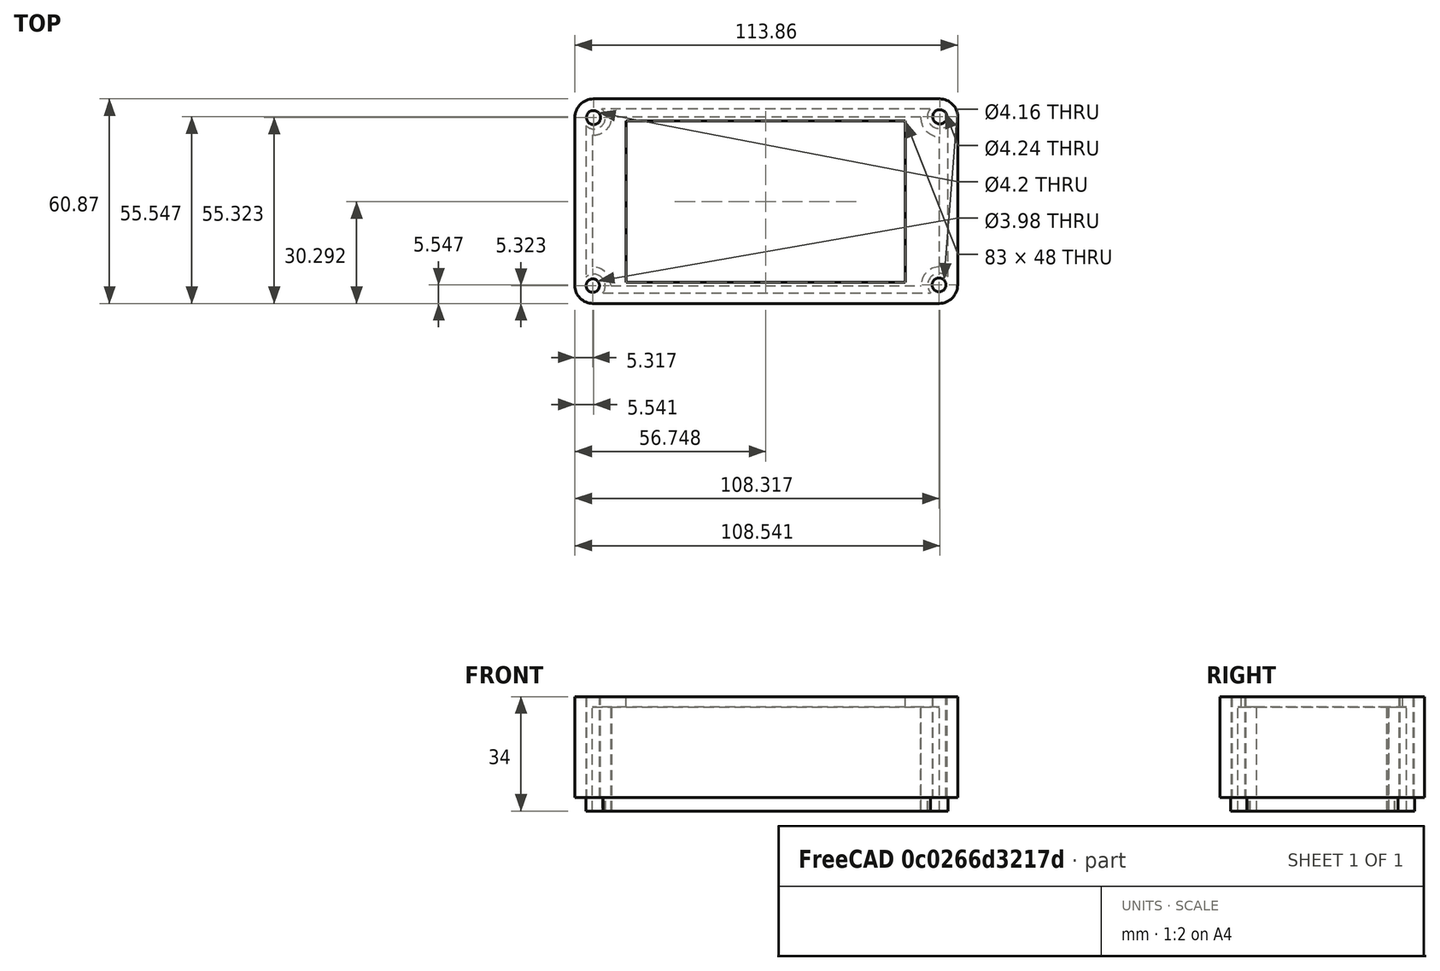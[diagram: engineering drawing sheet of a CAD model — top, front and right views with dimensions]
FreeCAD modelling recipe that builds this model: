
FCSTD DOCUMENT  (FreeCAD 0.18R4 (GitTag))
Label: uno
License: All rights reserved
LicenseURL: http://en.wikipedia.org/wiki/All_rights_reserved
objects: Sketcher::SketchObject×4, PartDesign::Pad×2, PartDesign::Pocket×2, PartDesign::Body×1, Mesh::Feature×1
note: 13 computed .brp shape members not serialized (recipe doc carries the construction recipe); baked Part::Feature solids carry a one-line shape summary decoded from their .brp

FEATURE [Sketcher::SketchObject] Sketch
  MapMode = 5
  Support = -> [XY_Plane]
  sketch-geometry (12):
    g0: LineSegment StartX=5.03716 StartY=-0.785506 StartZ=0 EndX=108.037 EndY=-0.785506 EndZ=0
    g1: LineSegment StartX=113.579 StartY=4.75676 StartZ=0 EndX=113.579 EndY=54.7568 EndZ=0
    g2: LineSegment StartX=108.261 StartY=60.0751 StartZ=0 EndX=5.26104 EndY=60.0751 EndZ=0
    g3: LineSegment StartX=-0.281219 StartY=54.5329 StartZ=0 EndX=-0.281219 EndY=4.53287 EndZ=0
    g4: ArcOfCircle CenterX=5.26104 CenterY=54.5329 CenterZ=0 NormalX=0 NormalY=0 NormalZ=1 AngleXU=0 Radius=5.54226 StartAngle=1.5708 EndAngle=3.14159
    g5: ArcOfCircle CenterX=108.261 CenterY=54.7568 CenterZ=0 NormalX=0 NormalY=0 NormalZ=1 AngleXU=0 Radius=5.31838 StartAngle=3e-16 EndAngle=1.5708
    g6: ArcOfCircle CenterX=5.03716 CenterY=4.53287 CenterZ=0 NormalX=0 NormalY=0 NormalZ=1 AngleXU=0 Radius=5.31838 StartAngle=3.14159 EndAngle=4.71239
    g7: ArcOfCircle CenterX=108.037 CenterY=4.75676 CenterZ=0 NormalX=0 NormalY=0 NormalZ=1 AngleXU=0 Radius=5.54226 StartAngle=4.71239 EndAngle=6.28319
    g8: Circle CenterX=5.03716 CenterY=4.53287 CenterZ=0 NormalX=0 NormalY=0 NormalZ=1 AngleXU=0 Radius=1.9886
    g9: Circle CenterX=108.037 CenterY=4.75676 CenterZ=0 NormalX=0 NormalY=0 NormalZ=1 AngleXU=0 Radius=2.07806
    g10: Circle CenterX=5.26104 CenterY=54.5329 CenterZ=0 NormalX=0 NormalY=0 NormalZ=1 AngleXU=0 Radius=2.0986
    g11: Circle CenterX=108.261 CenterY=54.7568 CenterZ=0 NormalX=0 NormalY=0 NormalZ=1 AngleXU=0 Radius=2.12051
  constraints (19):
    c: Horizontal(g0)
    c: Horizontal(g2)
    c: Vertical(g1)
    c: Vertical(g3)
    c: Tangent(g2,g4) = -1.5708
    c: Tangent(g3,g4) = -1.5708
    c: Tangent(g2,g5) = -1.5708
    c: Tangent(g1,g5) = -1.5708
    c: Tangent(g0,g6) = -1.5708
    c: Tangent(g3,g6) = -1.5708
    c: Tangent(g1,g7) = -1.5708
    c: Tangent(g0,g7) = -1.5708
    c: DistanceY(g3,g3) = 50
    c: DistanceX(g2,g2) = 103
    c: DistanceX(g0,g0) = 103
    c: Coincident(g8,g6)
    c: Coincident(g9,g7)
    c: Coincident(g10,g4)
    c: Coincident(g11,g5)
FEATURE [PartDesign::Pad] Pad
  Length = 30
  Length2 = 100
  Profile = -> Sketch
  Refine = true
  Type = 0
FEATURE [Sketcher::SketchObject] Sketch001
  MapMode = 5
  Placement = pos=(0,0,0) rot=(1,0,0;3.14159rad)
  Support = -> [Pad]
  sketch-geometry (8):
    g0: LineSegment StartX=8.07072 StartY=-2.40627 StartZ=0 EndX=105.522 EndY=-2.40627 EndZ=0
    g1: LineSegment StartX=110.632 StartY=-7.15837 StartZ=0 EndX=110.632 EndY=-52.2009 EndZ=0
    g2: LineSegment StartX=105.323 StartY=-57.0385 StartZ=0 EndX=7.70864 EndY=-57.0385 EndZ=0
    g3: LineSegment StartX=2.9358 StartY=-52.1381 StartZ=0 EndX=2.9358 EndY=-7.09059 EndZ=0
    g4: ArcOfCircle CenterX=5.24678 CenterY=-4.46729 CenterZ=0 NormalX=0 NormalY=0 NormalZ=1 AngleXU=0 Radius=3.49605 StartAngle=3.9902 EndAngle=6.91366
    g5: ArcOfCircle CenterX=5.36355 CenterY=-54.5481 CenterZ=0 NormalX=0 NormalY=0 NormalZ=1 AngleXU=0 Radius=3.42079 StartAngle=5.46773 EndAngle=8.64306
    g6: ArcOfCircle CenterX=108.149 CenterY=-4.7048 CenterZ=0 NormalX=0 NormalY=0 NormalZ=1 AngleXU=0 Radius=3.49068 StartAngle=2.4228 EndAngle=5.50373
    g7: ArcOfCircle CenterX=108.199 CenterY=-54.8624 CenterZ=0 NormalX=0 NormalY=0 NormalZ=1 AngleXU=0 Radius=3.60613 StartAngle=0.830175 EndAngle=3.78941
  constraints (12):
    c: Horizontal(g0)
    c: Horizontal(g2)
    c: Vertical(g1)
    c: Vertical(g3)
    c: Coincident(g1,g7)
    c: Coincident(g2,g7)
    c: Coincident(g3,g5)
    c: Coincident(g2,g5)
    c: Coincident(g3,g4)
    c: Coincident(g0,g4)
    c: Coincident(g0,g6)
    c: Coincident(g1,g6)
FEATURE [PartDesign::Pad] Pad001
  BaseFeature = -> Pad
  Length = 4
  Length2 = 100
  Profile = -> Sketch001
  Refine = true
  Type = 0
FEATURE [Sketcher::SketchObject] Sketch002
  MapMode = 5
  Placement = pos=(0,0,-4) rot=(1,0,0;3.14159rad)
  Support = -> [Pad001]
  sketch-geometry (8):
    g0: LineSegment StartX=10.4462 StartY=-4.55807 StartZ=0 EndX=102.685 EndY=-4.55807 EndZ=0
    g1: LineSegment StartX=108.209 StartY=-10.0822 StartZ=0 EndX=108.209 EndY=-48.8396 EndZ=0
    g2: LineSegment StartX=102.607 StartY=-54.6244 StartZ=0 EndX=10.7091 EndY=-54.6244 EndZ=0
    g3: LineSegment StartX=4.88695 StartY=-49.3458 StartZ=0 EndX=4.88695 EndY=-10.1173 EndZ=0
    g4: ArcOfCircle CenterX=4.88695 CenterY=-4.55807 CenterZ=0 NormalX=0 NormalY=0 NormalZ=1 AngleXU=0 Radius=5.55923 StartAngle=4.71239 EndAngle=6.28319
    g5: ArcOfCircle CenterX=108.209 CenterY=-4.55807 CenterZ=0 NormalX=0 NormalY=0 NormalZ=1 AngleXU=0 Radius=5.52413 StartAngle=3.14159 EndAngle=4.71239
    g6: ArcOfCircle CenterX=108.209 CenterY=-54.4446 CenterZ=0 NormalX=0 NormalY=0 NormalZ=1 AngleXU=0 Radius=5.60501 StartAngle=1.5708 EndAngle=3.17368
    g7: ArcOfCircle CenterX=5.24286 CenterY=-54.8034 CenterZ=0 NormalX=0 NormalY=0 NormalZ=1 AngleXU=0 Radius=5.46919 StartAngle=0.0327351 EndAngle=1.63592
  constraints (12):
    c: Horizontal(g0)
    c: Horizontal(g2)
    c: Vertical(g1)
    c: Vertical(g3)
    c: Coincident(g3,g7)
    c: Coincident(g2,g7)
    c: Coincident(g2,g6)
    c: Coincident(g1,g6)
    c: Coincident(g0,g5)
    c: Coincident(g1,g5)
    c: Coincident(g3,g4)
    c: Coincident(g0,g4)
FEATURE [PartDesign::Pocket] Pocket
  BaseFeature = -> Pad001
  Length = 31
  Length2 = 100
  Profile = -> Sketch002
  Refine = true
  Type = 0
FEATURE [Sketcher::SketchObject] Sketch003
  MapMode = 5
  Placement = pos=(0,0,27) rot=(1,0,0;3.14159rad)
  Support = -> [Pocket]
  sketch-geometry (4):
    g0: LineSegment StartX=14.9678 StartY=-5.50156 StartZ=0 EndX=97.9678 EndY=-5.50156 EndZ=0
    g1: LineSegment StartX=97.9678 StartY=-5.50156 StartZ=0 EndX=97.9678 EndY=-53.5016 EndZ=0
    g2: LineSegment StartX=97.9678 StartY=-53.5016 StartZ=0 EndX=14.9678 EndY=-53.5016 EndZ=0
    g3: LineSegment StartX=14.9678 StartY=-53.5016 StartZ=0 EndX=14.9678 EndY=-5.50156 EndZ=0
  constraints (10):
    c: Coincident(g0,g1)
    c: Coincident(g1,g2)
    c: Coincident(g2,g3)
    c: Coincident(g3,g0)
    c: Horizontal(g0)
    c: Horizontal(g2)
    c: Vertical(g1)
    c: Vertical(g3)
    c: DistanceY(g1,g1) = 48
    c: DistanceX(g2,g2) = 83
FEATURE [PartDesign::Pocket] Pocket001
  BaseFeature = -> Pocket
  Length = 3
  Length2 = 100
  Profile = -> Sketch003
  Refine = true
  Type = 0
FEATURE [PartDesign::Body] Body
  Group = -> [Sketch,Pad,Sketch001,Pad001,Sketch002,Pocket,Sketch003,Pocket001]
  Origin = -> Origin
  Tip = -> Pocket001
FEATURE [Mesh::Feature] Mesh  label="Pocket001 (Meshed)"
